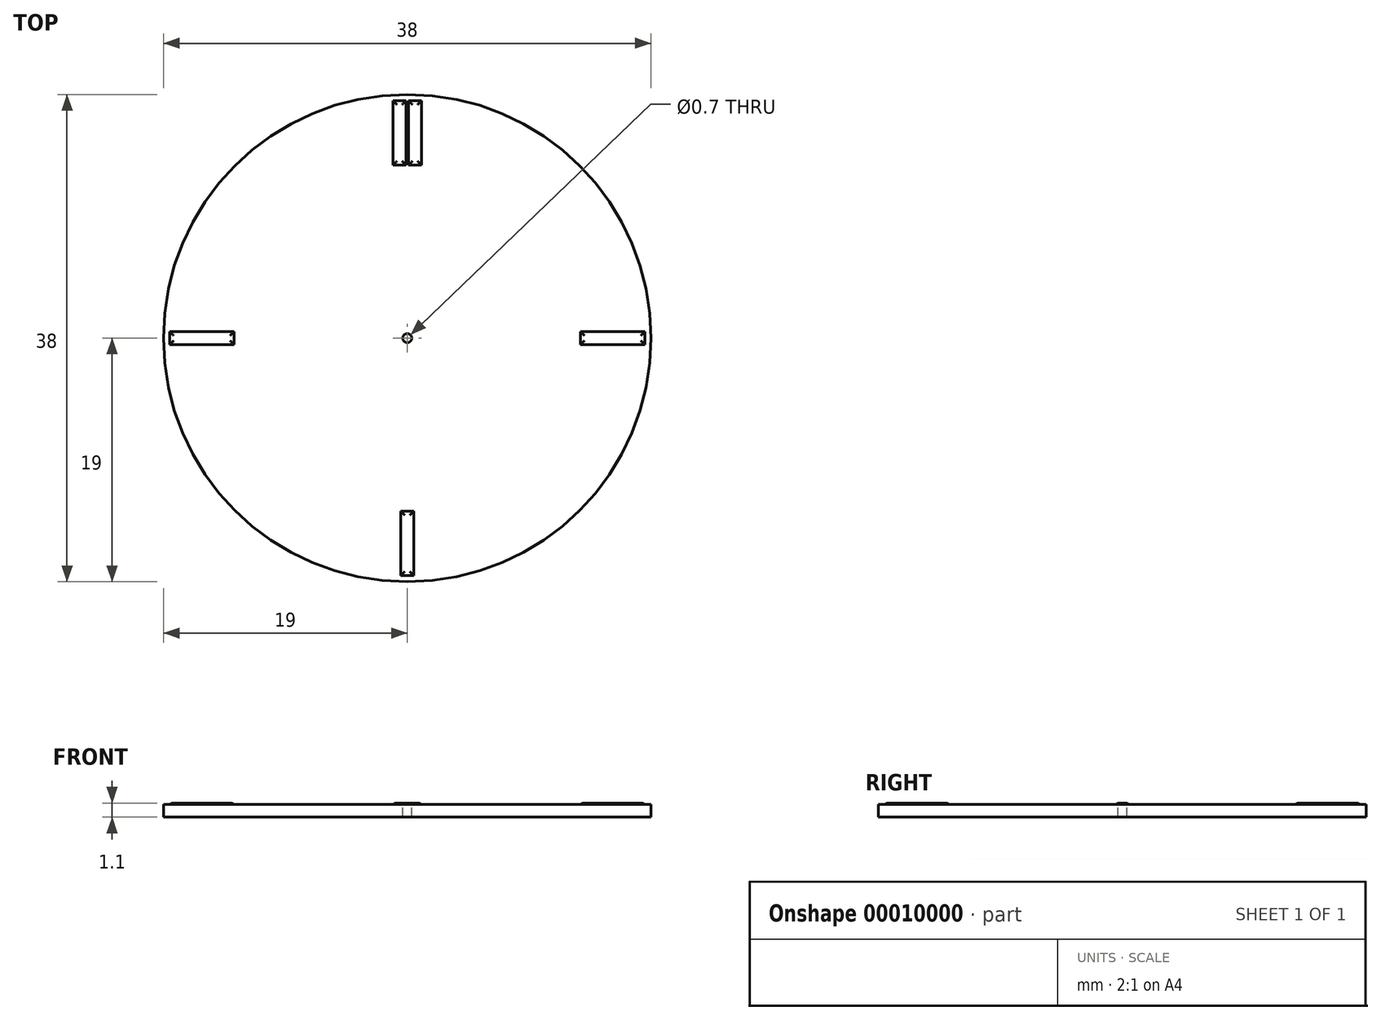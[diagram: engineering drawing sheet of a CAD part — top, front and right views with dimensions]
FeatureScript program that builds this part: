
annotation { "Feature Type Name" : "Feature", "Feature Type Description" : "" }
export const myFeature = defineFeature(function(context is Context, id is Id, definition is map)
    precondition{}
    {
        {
            var Q0;
            Q0=qCreatedBy(makeId("Top.planeOp"),FACE);
            var sketch = newSketch(context, id + "F0", { "sketchPlane" : qUnion([Q0])});
            skCircle(sketch, "E0", {"center": v(0, 0) * mm, "radius": 19 * mm});
            skSolve(sketch);
        }
        {
            var Q0;
            Q0 = qSketchRegion(id + "F0", true);
            extrude(context, id + "F1", {"entities" : qUnion([Q0]), "depth" : 1 * mm});
        }
        {
            var Q0;
            Q0=makeQuery(id+"F1.opExtrude","CAP_FACE",FACE,{"disambiguationData":[OSD([sQuery(id+"F0.wireOp",EDGE,"E0")])],"isStart":false});
            var sketch = newSketch(context, id + "F2", { "sketchPlane" : qUnion([Q0])});
            skLineSegment(sketch, "E1.bottom", {"start": v(-1.1, 18.5) * mm, "end": v(-0.1, 18.5) * mm});
            skLineSegment(sketch, "E1.top", {"start": v(-1.1, 13.5) * mm, "end": v(-0.1, 13.5) * mm});
            skLineSegment(sketch, "E1.left", {"start": v(-1.1, 18.5) * mm, "end": v(-1.1, 13.5) * mm});
            skLineSegment(sketch, "E1.right", {"start": v(-0.1, 18.5) * mm, "end": v(-0.1, 13.5) * mm});
            skLineSegment(sketch, "E2.bottom", {"start": v(0.1, 18.5) * mm, "end": v(1.1, 18.5) * mm});
            skLineSegment(sketch, "E2.top", {"start": v(0.1, 13.5) * mm, "end": v(1.1, 13.5) * mm});
            skLineSegment(sketch, "E2.left", {"start": v(0.1, 18.5) * mm, "end": v(0.1, 13.5) * mm});
            skLineSegment(sketch, "E2.right", {"start": v(1.1, 18.5) * mm, "end": v(1.1, 13.5) * mm});
            skLineSegment(sketch, "E3.bottom", {"start": v(13.5, 0.5) * mm, "end": v(18.5, 0.5) * mm});
            skLineSegment(sketch, "E3.top", {"start": v(13.5, -0.5) * mm, "end": v(18.5, -0.5) * mm});
            skLineSegment(sketch, "E3.left", {"start": v(13.5, 0.5) * mm, "end": v(13.5, -0.5) * mm});
            skLineSegment(sketch, "E3.right", {"start": v(18.5, 0.5) * mm, "end": v(18.5, -0.5) * mm});
            skLineSegment(sketch, "E4.bottom", {"start": v(-18.5, 0.5) * mm, "end": v(-13.5, 0.5) * mm});
            skLineSegment(sketch, "E4.top", {"start": v(-18.5, -0.5) * mm, "end": v(-13.5, -0.5) * mm});
            skLineSegment(sketch, "E4.left", {"start": v(-18.5, 0.5) * mm, "end": v(-18.5, -0.5) * mm});
            skLineSegment(sketch, "E4.right", {"start": v(-13.5, 0.5) * mm, "end": v(-13.5, -0.5) * mm});
            skLineSegment(sketch, "E5.bottom", {"start": v(-0.5, -13.5) * mm, "end": v(0.5, -13.5) * mm});
            skLineSegment(sketch, "E5.top", {"start": v(-0.5, -18.5) * mm, "end": v(0.5, -18.5) * mm});
            skLineSegment(sketch, "E5.left", {"start": v(-0.5, -13.5) * mm, "end": v(-0.5, -18.5) * mm});
            skLineSegment(sketch, "E5.right", {"start": v(0.5, -13.5) * mm, "end": v(0.5, -18.5) * mm});
            skSolve(sketch);
        }
        {
            var Q0;
            Q0 = qSketchRegion(id + "F2", true);
            extrude(context, id + "F3", {"entities" : qUnion([Q0]), "operationType" : NewBodyOperationType.ADD, "depth" : 0.1 * mm});
        }
        {
            var Q0;
            Q0=makeQuery(id+"F3.opExtrude","CAP_FACE",FACE,{"disambiguationData":[OSD([sQuery(id+"F2.wireOp",EDGE,"E4.bottom"),sQuery(id+"F2.wireOp",EDGE,"E4.top"),sQuery(id+"F2.wireOp",EDGE,"E4.left"),sQuery(id+"F2.wireOp",EDGE,"E4.right")])],"isStart":false});
            fillet(context, id + "F4", {"entities" : qUnion([Q0]), "radius" : 0.5 * mm, "tangentPropagation" : true, "allowEdgeOverflow" : false});
        }
        {
            var Q0;
            Q0=makeQuery(id+"F3.opExtrude","CAP_FACE",FACE,{"disambiguationData":[OSD([sQuery(id+"F2.wireOp",EDGE,"E1.bottom"),sQuery(id+"F2.wireOp",EDGE,"E1.top"),sQuery(id+"F2.wireOp",EDGE,"E1.left"),sQuery(id+"F2.wireOp",EDGE,"E1.right")])],"isStart":false});
            var Q1;
            Q1=makeQuery(id+"F3.opExtrude","CAP_FACE",FACE,{"disambiguationData":[OSD([sQuery(id+"F2.wireOp",EDGE,"E2.bottom"),sQuery(id+"F2.wireOp",EDGE,"E2.top"),sQuery(id+"F2.wireOp",EDGE,"E2.left"),sQuery(id+"F2.wireOp",EDGE,"E2.right")])],"isStart":false});
            var Q2;
            Q2=makeQuery(id+"F3.opExtrude","CAP_FACE",FACE,{"disambiguationData":[OSD([sQuery(id+"F2.wireOp",EDGE,"E3.bottom"),sQuery(id+"F2.wireOp",EDGE,"E3.top"),sQuery(id+"F2.wireOp",EDGE,"E3.left"),sQuery(id+"F2.wireOp",EDGE,"E3.right")])],"isStart":false});
            var Q3;
            Q3=makeQuery(id+"F3.opExtrude","CAP_FACE",FACE,{"disambiguationData":[OSD([sQuery(id+"F2.wireOp",EDGE,"E5.bottom"),sQuery(id+"F2.wireOp",EDGE,"E5.top"),sQuery(id+"F2.wireOp",EDGE,"E5.left"),sQuery(id+"F2.wireOp",EDGE,"E5.right")])],"isStart":false});
            fillet(context, id + "F5", {"entities" : qUnion([Q0, Q1, Q2, Q3]), "radius" : 0.5 * mm, "tangentPropagation" : true, "allowEdgeOverflow" : false});
        }
        {
            var Q0;
            Q0=makeQuery(id+"F1.opExtrude","CAP_FACE",FACE,{"disambiguationData":[OSD([sQuery(id+"F0.wireOp",EDGE,"E0")])],"isStart":false});
            var sketch = newSketch(context, id + "F6", { "sketchPlane" : qUnion([Q0])});
            skCircle(sketch, "E6", {"center": v(0, 0) * mm, "radius": 0.35 * mm});
            skSolve(sketch);
        }
        {
            var Q0;
            Q0 = qSketchRegion(id + "F6", true);
            extrude(context, id + "F7", {"entities" : qUnion([Q0]), "operationType" : NewBodyOperationType.REMOVE, "oppositeDirection" : true, "depth" : 25 * mm});
        }
    });
